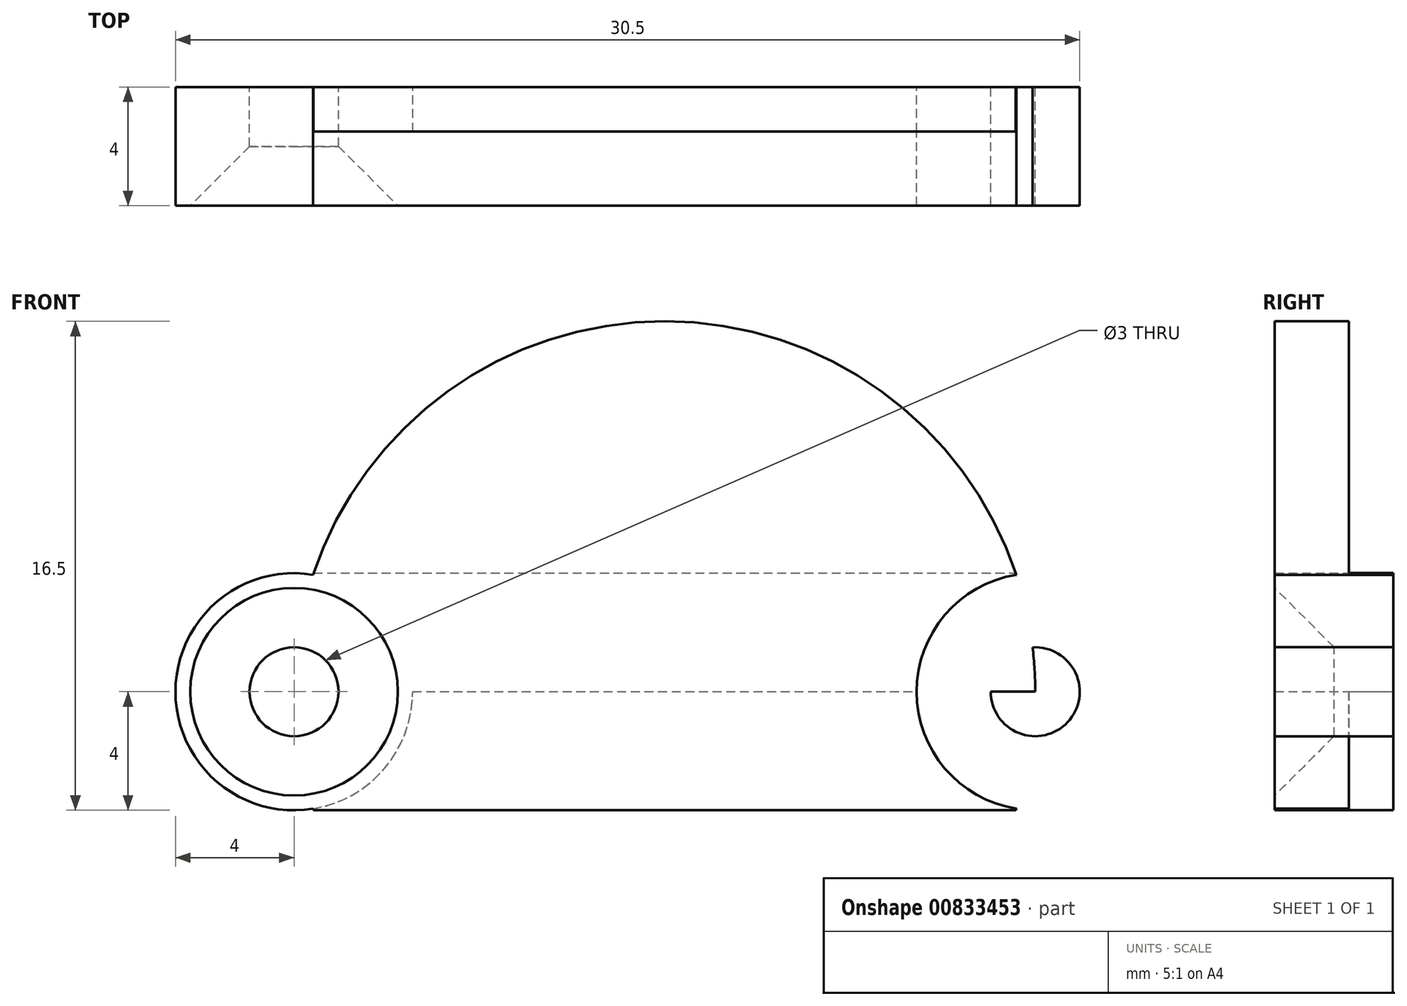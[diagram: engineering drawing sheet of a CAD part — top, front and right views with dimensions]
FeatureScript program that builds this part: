
annotation { "Feature Type Name" : "Feature", "Feature Type Description" : "" }
export const myFeature = defineFeature(function(context is Context, id is Id, definition is map)
    precondition{}
    {
        {
            var Q0;
            Q0=qCreatedBy(makeId("Front.planeOp"),FACE);
            var sketch = newSketch(context, id + "F0", { "sketchPlane" : qUnion([Q0])});
            skCircle(sketch, "E0", {"center": v(0, 0) * mm, "radius": 12.5 * mm});
            skCircle(sketch, "E1", {"center": v(12.5, 0) * mm, "radius": 1.5 * mm});
            skCircle(sketch, "E2", {"center": v(-12.5, 0) * mm, "radius": 1.5 * mm});
            skCircle(sketch, "E3", {"center": v(12.5, 0) * mm, "radius": 4 * mm});
            skCircle(sketch, "E4", {"center": v(-12.5, 0) * mm, "radius": 4 * mm});
            skLineSegment(sketch, "E5", {"start": v(-12.5, 0) * mm, "end": v(12.5, 0) * mm});
            skLineSegment(sketch, "E6", {"start": v(-12.5, 4) * mm, "end": v(12.5, 4) * mm});
            skLineSegment(sketch, "E7.MirrorCS", {"start": v(-12.5, -4) * mm, "end": v(12.5, -4) * mm});
            skSolve(sketch);
        }
        {
            var Q0;
            {var subQ0=sQuery(id+"F0.wireOp",EDGE,"E4");var subQ2=sQuery(id+"F0.wireOp",EDGE,"E0");var subQ3=makeQuery(id+"F0.imprint","INTERSECT",VERTEX,{"disambiguationData":[OD(0.0)],"derivedFrom":[subQ2,subQ0]});Q0=makeQuery(id+"F0.imprint","IMPRINT",FACE,{"disambiguationData":[TD([[makeQuery(id+"F0.imprint","IMPRINT",EDGE,{"disambiguationData":[TD([[subQ3,-1.0]])],"derivedFrom":subQ2}),-1.0]])]});}
            var Q1;
            {var subQ0=sQuery(id+"F0.wireOp",EDGE,"E4");var subQ1=sQuery(id+"F0.wireOp",EDGE,"E0");var subQ2=makeQuery(id+"F0.imprint","INTERSECT",VERTEX,{"disambiguationData":[OD(0.0)],"derivedFrom":[subQ1,subQ0]});Q1=makeQuery(id+"F0.imprint","IMPRINT",FACE,{"disambiguationData":[TD([[makeQuery(id+"F0.imprint","IMPRINT",EDGE,{"disambiguationData":[TD([[subQ2,-1.0]])],"derivedFrom":subQ1}),1.0]])]});}
            var Q2;
            {var subQ0=sQuery(id+"F0.wireOp",EDGE,"E2");var subQ1=sQuery(id+"F0.wireOp",EDGE,"E0");var subQ2=makeQuery(id+"F0.imprint","INTERSECT",VERTEX,{"disambiguationData":[OD(1.0)],"derivedFrom":[subQ1,subQ0]});Q2=makeQuery(id+"F0.imprint","IMPRINT",FACE,{"disambiguationData":[TD([[makeQuery(id+"F0.imprint","IMPRINT",EDGE,{"disambiguationData":[TD([[subQ2,-1.0]])],"derivedFrom":subQ1}),1.0]])]});}
            var Q3;
            {var subQ1=sQuery(id+"F0.wireOp",EDGE,"E0");var subQ5=sQuery(id+"F0.wireOp",EDGE,"E7.MirrorCS");var subQ10=makeQuery(id+"F0.imprint","INTERSECT",VERTEX,{"disambiguationData":[OD(0.0)],"derivedFrom":[subQ1,subQ5]});Q3=makeQuery(id+"F0.imprint","IMPRINT",FACE,{"disambiguationData":[TD([[makeQuery(id+"F0.imprint","IMPRINT",EDGE,{"disambiguationData":[TD([[subQ10,1.0]])],"derivedFrom":subQ1}),1.0]])]});}
            var Q4;
            {var subQ1=sQuery(id+"F0.wireOp",EDGE,"E0");var subQ5=sQuery(id+"F0.wireOp",EDGE,"E6");var subQ6=makeQuery(id+"F0.imprint","INTERSECT",VERTEX,{"disambiguationData":[OD(0.0)],"derivedFrom":[subQ1,subQ5]});Q4=makeQuery(id+"F0.imprint","IMPRINT",FACE,{"disambiguationData":[TD([[makeQuery(id+"F0.imprint","IMPRINT",EDGE,{"disambiguationData":[TD([[subQ6,1.0]])],"derivedFrom":subQ1}),1.0]])]});}
            var Q5;
            {var subQ0=sQuery(id+"F0.wireOp",EDGE,"E1");var subQ1=sQuery(id+"F0.wireOp",EDGE,"E0");var subQ2=makeQuery(id+"F0.imprint","INTERSECT",VERTEX,{"disambiguationData":[OD(0.0)],"derivedFrom":[subQ1,subQ0]});Q5=makeQuery(id+"F0.imprint","IMPRINT",FACE,{"disambiguationData":[TD([[makeQuery(id+"F0.imprint","IMPRINT",EDGE,{"disambiguationData":[TD([[subQ2,-1.0]])],"derivedFrom":subQ1}),1.0]])]});}
            var Q6;
            {var subQ0=sQuery(id+"F0.wireOp",EDGE,"E3");var subQ1=sQuery(id+"F0.wireOp",EDGE,"E0");var subQ2=makeQuery(id+"F0.imprint","INTERSECT",VERTEX,{"disambiguationData":[OD(1.0)],"derivedFrom":[subQ1,subQ0]});Q6=makeQuery(id+"F0.imprint","IMPRINT",FACE,{"disambiguationData":[TD([[makeQuery(id+"F0.imprint","IMPRINT",EDGE,{"disambiguationData":[TD([[subQ2,-1.0]])],"derivedFrom":subQ1}),1.0]])]});}
            var Q7;
            {var subQ2=sQuery(id+"F0.wireOp",EDGE,"E0");var subQ5=sQuery(id+"F0.wireOp",EDGE,"E1");var subQ7=makeQuery(id+"F0.imprint","INTERSECT",VERTEX,{"disambiguationData":[OD(0.0)],"derivedFrom":[subQ2,subQ5]});Q7=makeQuery(id+"F0.imprint","IMPRINT",FACE,{"disambiguationData":[TD([[makeQuery(id+"F0.imprint","IMPRINT",EDGE,{"disambiguationData":[TD([[subQ7,-1.0]])],"derivedFrom":subQ2}),-1.0]])]});}
            extrude(context, id + "F1", {"entities" : qUnion([Q0, Q1, Q2, Q3, Q4, Q5, Q6, Q7]), "depth" : 4 * mm, "offsetDistance" : 25 * mm});
        }
        {
            var Q0;
            {var subQ1=sQuery(id+"F0.wireOp",EDGE,"E0");var subQ5=sQuery(id+"F0.wireOp",EDGE,"E7.MirrorCS");var subQ10=makeQuery(id+"F0.imprint","INTERSECT",VERTEX,{"disambiguationData":[OD(0.0)],"derivedFrom":[subQ1,subQ5]});Q0=makeQuery(id+"F0.imprint","IMPRINT",FACE,{"disambiguationData":[TD([[makeQuery(id+"F0.imprint","IMPRINT",EDGE,{"disambiguationData":[TD([[subQ10,1.0]])],"derivedFrom":subQ1}),1.0]])]});}
            var Q1;
            {var subQ1=sQuery(id+"F0.wireOp",EDGE,"E0");var subQ5=sQuery(id+"F0.wireOp",EDGE,"E6");var subQ6=makeQuery(id+"F0.imprint","INTERSECT",VERTEX,{"disambiguationData":[OD(0.0)],"derivedFrom":[subQ1,subQ5]});Q1=makeQuery(id+"F0.imprint","IMPRINT",FACE,{"disambiguationData":[TD([[makeQuery(id+"F0.imprint","IMPRINT",EDGE,{"disambiguationData":[TD([[subQ6,1.0]])],"derivedFrom":subQ1}),1.0]])]});}
            extrude(context, id + "F2", {"entities" : qUnion([Q0, Q1]), "operationType" : NewBodyOperationType.REMOVE, "depth" : 1.5 * mm, "offsetDistance" : 25 * mm});
        }
        {
            var Q0;
            Q0=makeQuery(id+"F1.opExtrude","CAP_EDGE",EDGE,{"disambiguationData":[OSD([sQuery(id+"F0.wireOp",EDGE,"E2")])],"isStart":false});
            var Q1;
            Q1=makeQuery(id+"F1.opExtrude","CAP_EDGE",EDGE,{"disambiguationData":[OSD([sQuery(id+"F0.wireOp",EDGE,"E1")])],"isStart":false});
            chamfer(context, id + "F3", {"entities" : qUnion([Q0, Q1]), "width" : 2 * mm, "tangentPropagation" : true});
        }
    });
